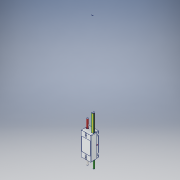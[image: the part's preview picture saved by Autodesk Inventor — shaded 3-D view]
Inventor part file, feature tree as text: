
AUTODESK INVENTOR PART (.ipt)
format: ipt  version: 2018 (Build 220112000, 112)  size: 2,402,304 bytes
history: native  units: in
note: dims shown in document units (in); Inventor stores cm internally (conversion verified against a paired STEP export)
features: extrude x1, sketch x1, boolean_combine x1
ambient origin geometry x8: Origin, YZ Plane, XZ Plane, XY Plane, X Axis, Y Axis, Z Axis, Center Point
bodies: Solid1 (feature_tree)
feature tree (3):
  extrude  "Extrusion2"  TaperAngle=0.0deg  [1 undecoded]
  sketch  "Sketch1"  dims[d0=1.0in d1=0.0in d2=0.0in d4=0.0in d5=1.0in d6=0.0in d7=0.0in d10=0.5in d12=0.0in d13=0.0in d14=1.0in d15=0.5in d16=1.0in d17=0.0in]
  boolean_combine  "Combine11"
note: 1 required parameter value undecoded (feature->parameter linkage not recoverable at this tier; creation-order binding heuristic only, values carry confidence <= 0.55)
